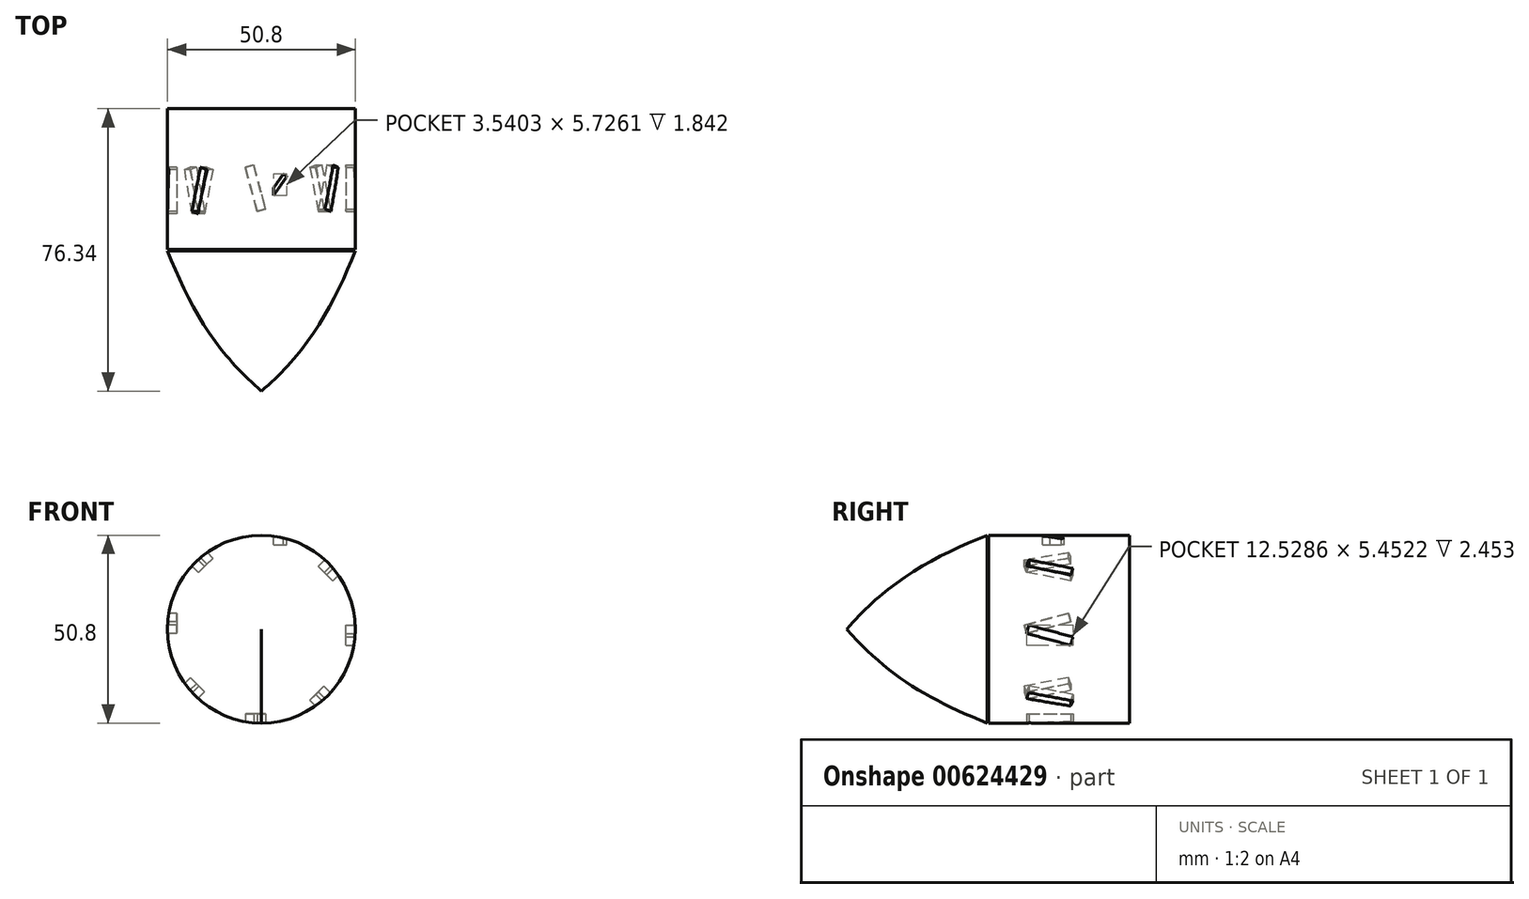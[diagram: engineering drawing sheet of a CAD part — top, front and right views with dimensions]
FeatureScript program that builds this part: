
annotation { "Feature Type Name" : "Feature", "Feature Type Description" : "" }
export const myFeature = defineFeature(function(context is Context, id is Id, definition is map)
    precondition{}
    {
        {
            var Q0;
            Q0=qCreatedBy(makeId("Front.planeOp"),FACE);
            var sketch = newSketch(context, id + "F0", { "sketchPlane" : qUnion([Q0])});
            skCircle(sketch, "E0", {"center": v(0, 0) * mm, "radius": 25.4 * mm});
            skSolve(sketch);
        }
        {
            var Q0;
            Q0=makeQuery(id+"F0.imprint","IMPRINT",FACE,{"disambiguationData":[TD([[makeQuery(id+"F0.imprint","IMPRINT",EDGE,{"derivedFrom":sQuery(id+"F0.wireOp",EDGE,"E0")}),1.0]])]});
            extrude(context, id + "F1", {"entities" : qUnion([Q0]), "depth" : 38.1 * mm, "offsetDistance" : 25.4 * mm});
        }
        {
            var Q0;
            Q0=qCreatedBy(makeId("Right.planeOp"),FACE);
            var sketch = newSketch(context, id + "F2", { "sketchPlane" : qUnion([Q0])});
            skLineSegment(sketch, "E1", {"start": v(-76.34, 0) * mm, "end": v(-38.37, 0) * mm});
            skLineSegment(sketch, "E2", {"start": v(-38.37, 0) * mm, "end": v(-38.37, 25.4) * mm});
            skLineSegment(sketch, "E3", {"start": v(-38.37, 0) * mm, "end": v(-38.37, -25.4) * mm});
            skFitSpline(sketch, "E4", {"points": [v(-38.37, -25.4) * mm, v(-76.34, 0) * mm], "startDerivative": vector(-48.65, 19.21) * mm, "endDerivative": vector(-31.18, 36.31) * mm});
            skSolve(sketch);
        }
        {
            var Q0;
            Q0=makeQuery(id+"F2.imprint","IMPRINT",FACE,{"disambiguationData":[TD([[makeQuery(id+"F2.imprint","IMPRINT",EDGE,{"derivedFrom":sQuery(id+"F2.wireOp",EDGE,"E1")}),-1.0]])]});
            var Q1;
            Q1=sQuery(id+"F2.wireOp",EDGE,"E1");
            revolve(context, id + "F3", {"entities" : qUnion([Q0]), "axis" : qUnion([Q1]), "revolveType" : RevolveType.FULL});
        }
        {
            var Q0;
            Q0=qCreatedBy(makeId("Right.planeOp"),FACE);
            cPlane(context, id + "F4", {"entities" : qUnion([Q0]), "cplaneType" : CPlaneType.OFFSET, "offset" : 25.4 * mm, "width" : 152.4 * mm, "height" : 152.4 * mm});
        }
        {
            var Q0;
            Q0=qCreatedBy(makeId("Right.planeOp"),FACE);
            cPlane(context, id + "F5", {"entities" : qUnion([Q0]), "cplaneType" : CPlaneType.OFFSET, "offset" : 25.4 * mm, "oppositeDirection" : true, "width" : 152.4 * mm, "height" : 152.4 * mm});
        }
        {
            var Q0;
            Q0=qCreatedBy(makeId("Top.planeOp"),FACE);
            cPlane(context, id + "F6", {"entities" : qUnion([Q0]), "cplaneType" : CPlaneType.OFFSET, "offset" : 25.4 * mm, "width" : 152.4 * mm, "height" : 152.4 * mm});
        }
        {
            var Q0;
            Q0=qCreatedBy(makeId("Top.planeOp"),FACE);
            cPlane(context, id + "F7", {"entities" : qUnion([Q0]), "cplaneType" : CPlaneType.OFFSET, "offset" : 25.4 * mm, "oppositeDirection" : true, "width" : 152.4 * mm, "height" : 152.4 * mm});
        }
        {
            var Q0;
            Q0=qCreatedBy(makeId("Right.planeOp"),FACE);
            var Q1;
            Q1=qCreatedBy(makeId("Top.planeOp"),FACE);
            cPlane(context, id + "F8", {"entities" : qUnion([Q0, Q1]), "cplaneType" : CPlaneType.MID_PLANE, "offset" : 25.4 * mm, "width" : 152.4 * mm, "height" : 152.4 * mm});
        }
        {
            var Q0;
            Q0=qCreatedBy(makeId("Right.planeOp"),FACE);
            var Q1;
            Q1=qCreatedBy(makeId("Top.planeOp"),FACE);
            cPlane(context, id + "F9", {"entities" : qUnion([Q0, Q1]), "cplaneType" : CPlaneType.MID_PLANE, "offset" : 25.4 * mm, "flipAlignment" : true, "width" : 152.4 * mm, "height" : 152.4 * mm});
        }
        {
            var Q0;
            Q0=qCreatedBy(id+"F8.planeOp",FACE);
            cPlane(context, id + "F10", {"entities" : qUnion([Q0]), "cplaneType" : CPlaneType.OFFSET, "offset" : 25.4 * mm, "width" : 152.4 * mm, "height" : 152.4 * mm});
        }
        {
            var Q0;
            Q0=qCreatedBy(id+"F8.planeOp",FACE);
            cPlane(context, id + "F11", {"entities" : qUnion([Q0]), "cplaneType" : CPlaneType.OFFSET, "offset" : 25.4 * mm, "oppositeDirection" : true, "width" : 152.4 * mm, "height" : 152.4 * mm});
        }
        {
            var Q0;
            Q0=qCreatedBy(id+"F9.planeOp",FACE);
            cPlane(context, id + "F12", {"entities" : qUnion([Q0]), "cplaneType" : CPlaneType.OFFSET, "offset" : 25.4 * mm, "width" : 152.4 * mm, "height" : 152.4 * mm});
        }
        {
            var Q0;
            Q0=qCreatedBy(id+"F9.planeOp",FACE);
            cPlane(context, id + "F13", {"entities" : qUnion([Q0]), "cplaneType" : CPlaneType.OFFSET, "offset" : 25.4 * mm, "oppositeDirection" : true, "width" : 152.4 * mm, "height" : 152.4 * mm});
        }
        {
            var Q0;
            Q0=qCreatedBy(id+"F12.planeOp",FACE);
            var sketch = newSketch(context, id + "F14", { "sketchPlane" : qUnion([Q0])});
            skLineSegment(sketch, "E5.bottom", {"start": v(-15.84, -4.36) * mm, "end": v(-27.76, -1.17) * mm});
            skLineSegment(sketch, "E5.top", {"start": v(-15.23, -2.1) * mm, "end": v(-27.16, 1.09) * mm});
            skLineSegment(sketch, "E5.left", {"start": v(-15.84, -4.36) * mm, "end": v(-15.23, -2.1) * mm});
            skLineSegment(sketch, "E5.right", {"start": v(-27.76, -1.17) * mm, "end": v(-27.16, 1.09) * mm});
            skPoint(sketch, "E5.middle", {"position": v(-21.59, 0) * mm});
            skSolve(sketch);
        }
        {
            var Q0;
            Q0=qCreatedBy(id+"F11.planeOp",FACE);
            var sketch = newSketch(context, id + "F15", { "sketchPlane" : qUnion([Q0])});
            skLineSegment(sketch, "E6.bottom", {"start": v(-15.84, 2.03) * mm, "end": v(-27.76, -1.17) * mm});
            skLineSegment(sketch, "E6.top", {"start": v(-16.44, 4.28) * mm, "end": v(-28.37, 1.09) * mm});
            skLineSegment(sketch, "E6.left", {"start": v(-15.84, 2.03) * mm, "end": v(-16.44, 4.28) * mm});
            skLineSegment(sketch, "E6.right", {"start": v(-27.76, -1.17) * mm, "end": v(-28.37, 1.09) * mm});
            skPoint(sketch, "E6.middle", {"position": v(-21.59, 0) * mm});
            skSolve(sketch);
        }
        {
            var Q0;
            Q0=qCreatedBy(id+"F5.planeOp",FACE);
            var sketch = newSketch(context, id + "F16", { "sketchPlane" : qUnion([Q0])});
            skLineSegment(sketch, "E7.bottom", {"start": v(-15.84, 2.03) * mm, "end": v(-27.76, -1.17) * mm});
            skLineSegment(sketch, "E7.top", {"start": v(-16.44, 4.28) * mm, "end": v(-28.37, 1.09) * mm});
            skLineSegment(sketch, "E7.left", {"start": v(-15.84, 2.03) * mm, "end": v(-16.44, 4.28) * mm});
            skLineSegment(sketch, "E7.right", {"start": v(-27.76, -1.17) * mm, "end": v(-28.37, 1.09) * mm});
            skPoint(sketch, "E7.middle", {"position": v(-22.1, 1.56) * mm});
            skSolve(sketch);
        }
        {
            var Q0;
            Q0=qCreatedBy(id+"F13.planeOp",FACE);
            var sketch = newSketch(context, id + "F17", { "sketchPlane" : qUnion([Q0])});
            skLineSegment(sketch, "E8.bottom", {"start": v(-15.84, 2.03) * mm, "end": v(-27.76, -1.17) * mm});
            skLineSegment(sketch, "E8.top", {"start": v(-16.44, 4.28) * mm, "end": v(-28.37, 1.09) * mm});
            skLineSegment(sketch, "E8.left", {"start": v(-15.84, 2.03) * mm, "end": v(-16.44, 4.28) * mm});
            skLineSegment(sketch, "E8.right", {"start": v(-27.76, -1.17) * mm, "end": v(-28.37, 1.09) * mm});
            skPoint(sketch, "E8.middle", {"position": v(-22.1, 1.56) * mm});
            skSolve(sketch);
        }
        {
            var Q0;
            Q0=qCreatedBy(id+"F7.planeOp",FACE);
            var sketch = newSketch(context, id + "F18", { "sketchPlane" : qUnion([Q0])});
            skLineSegment(sketch, "E9.bottom", {"start": v(-1.17, -27.76) * mm, "end": v(-4.36, -15.84) * mm});
            skLineSegment(sketch, "E9.top", {"start": v(1.09, -27.16) * mm, "end": v(-2.1, -15.23) * mm});
            skLineSegment(sketch, "E9.left", {"start": v(-1.17, -27.76) * mm, "end": v(1.09, -27.16) * mm});
            skLineSegment(sketch, "E9.right", {"start": v(-4.36, -15.84) * mm, "end": v(-2.1, -15.23) * mm});
            skPoint(sketch, "E9.middle", {"position": v(-1.64, -21.5) * mm});
            skSolve(sketch);
        }
        {
            var Q0;
            Q0=qCreatedBy(id+"F10.planeOp",FACE);
            var sketch = newSketch(context, id + "F19", { "sketchPlane" : qUnion([Q0])});
            skLineSegment(sketch, "E10.bottom", {"start": v(-15.84, -4.36) * mm, "end": v(-27.76, -1.17) * mm});
            skLineSegment(sketch, "E10.top", {"start": v(-15.23, -2.1) * mm, "end": v(-27.16, 1.09) * mm});
            skLineSegment(sketch, "E10.left", {"start": v(-15.84, -4.36) * mm, "end": v(-15.23, -2.1) * mm});
            skLineSegment(sketch, "E10.right", {"start": v(-27.76, -1.17) * mm, "end": v(-27.16, 1.09) * mm});
            skPoint(sketch, "E10.middle", {"position": v(-21.5, -1.64) * mm});
            skSolve(sketch);
        }
        {
            var Q0;
            Q0=qCreatedBy(id+"F4.planeOp",FACE);
            var sketch = newSketch(context, id + "F20", { "sketchPlane" : qUnion([Q0])});
            skLineSegment(sketch, "E11.bottom", {"start": v(-15.84, -4.36) * mm, "end": v(-27.76, -1.17) * mm});
            skLineSegment(sketch, "E11.top", {"start": v(-15.23, -2.1) * mm, "end": v(-27.16, 1.09) * mm});
            skLineSegment(sketch, "E11.left", {"start": v(-15.84, -4.36) * mm, "end": v(-15.23, -2.1) * mm});
            skLineSegment(sketch, "E11.right", {"start": v(-27.76, -1.17) * mm, "end": v(-27.16, 1.09) * mm});
            skPoint(sketch, "E11.middle", {"position": v(-21.5, -1.64) * mm});
            skSolve(sketch);
        }
        {
            var Q0;
            Q0=qCreatedBy(id+"F6.planeOp",FACE);
            var sketch = newSketch(context, id + "F21", { "sketchPlane" : qUnion([Q0])});
            skLineSegment(sketch, "E12.bottom", {"start": v(-1.17, -27.76) * mm, "end": v(5.91, -17.65) * mm});
            skLineSegment(sketch, "E12.top", {"start": v(0.75, -29.1) * mm, "end": v(7.83, -19) * mm});
            skLineSegment(sketch, "E12.left", {"start": v(-1.17, -27.76) * mm, "end": v(0.75, -29.1) * mm});
            skLineSegment(sketch, "E12.right", {"start": v(5.91, -17.65) * mm, "end": v(7.83, -19) * mm});
            skPoint(sketch, "E12.middle", {"position": v(3.33, -23.38) * mm});
            skLineSegment(sketch, "E13", {"start": v(3.33, -23.38) * mm, "end": v(3.33, -4.06) * mm});
            skLineSegment(sketch, "E14", {"start": v(3.33, -23.38) * mm, "end": v(6.87, -18.32) * mm});
            skLineSegment(sketch, "E15", {"start": v(6.87, -18.32) * mm, "end": v(14.25, -7.78) * mm});
            skSolve(sketch);
        }
        {
            var Q0;
            Q0=makeQuery(id+"F16.imprint","IMPRINT",FACE,{"disambiguationData":[TD([[makeQuery(id+"F16.imprint","IMPRINT",EDGE,{"derivedFrom":sQuery(id+"F16.wireOp",EDGE,"E7.bottom")}),-1.0]])]});
            extrude(context, id + "F22", {"entities" : qUnion([Q0]), "operationType" : NewBodyOperationType.REMOVE, "depth" : 2.54 * mm, "offsetDistance" : 25.4 * mm});
        }
        {
            var Q0;
            Q0=makeQuery(id+"F15.imprint","IMPRINT",FACE,{"disambiguationData":[TD([[makeQuery(id+"F15.imprint","IMPRINT",EDGE,{"derivedFrom":sQuery(id+"F15.wireOp",EDGE,"E6.bottom")}),-1.0]])]});
            extrude(context, id + "F23", {"entities" : qUnion([Q0]), "operationType" : NewBodyOperationType.REMOVE, "depth" : 2.54 * mm, "offsetDistance" : 25.4 * mm});
        }
        {
            var Q0;
            Q0=makeQuery(id+"F21.imprint","IMPRINT",FACE,{"disambiguationData":[TD([[makeQuery(id+"F21.imprint","IMPRINT",EDGE,{"derivedFrom":sQuery(id+"F21.wireOp",EDGE,"E12.bottom")}),-1.0]])]});
            extrude(context, id + "F24", {"entities" : qUnion([Q0]), "operationType" : NewBodyOperationType.REMOVE, "oppositeDirection" : true, "depth" : 2.54 * mm, "offsetDistance" : 25.4 * mm});
        }
        {
            var Q0;
            Q0=makeQuery(id+"F14.imprint","IMPRINT",FACE,{"disambiguationData":[TD([[makeQuery(id+"F14.imprint","IMPRINT",EDGE,{"derivedFrom":sQuery(id+"F14.wireOp",EDGE,"E5.bottom")}),-1.0]])]});
            extrude(context, id + "F25", {"entities" : qUnion([Q0]), "operationType" : NewBodyOperationType.REMOVE, "oppositeDirection" : true, "depth" : 2.54 * mm, "offsetDistance" : 25.4 * mm});
        }
        {
            var Q0;
            Q0=makeQuery(id+"F20.imprint","IMPRINT",FACE,{"disambiguationData":[TD([[makeQuery(id+"F20.imprint","IMPRINT",EDGE,{"derivedFrom":sQuery(id+"F20.wireOp",EDGE,"E11.bottom")}),-1.0]])]});
            extrude(context, id + "F26", {"entities" : qUnion([Q0]), "operationType" : NewBodyOperationType.REMOVE, "oppositeDirection" : true, "depth" : 2.54 * mm, "offsetDistance" : 25.4 * mm});
        }
        {
            var Q0;
            Q0=makeQuery(id+"F19.imprint","IMPRINT",FACE,{"disambiguationData":[TD([[makeQuery(id+"F19.imprint","IMPRINT",EDGE,{"derivedFrom":sQuery(id+"F19.wireOp",EDGE,"E10.bottom")}),-1.0]])]});
            extrude(context, id + "F27", {"entities" : qUnion([Q0]), "operationType" : NewBodyOperationType.REMOVE, "oppositeDirection" : true, "depth" : 2.54 * mm, "offsetDistance" : 25.4 * mm});
        }
        {
            var Q0;
            Q0=makeQuery(id+"F18.imprint","IMPRINT",FACE,{"disambiguationData":[TD([[makeQuery(id+"F18.imprint","IMPRINT",EDGE,{"derivedFrom":sQuery(id+"F18.wireOp",EDGE,"E9.bottom")}),-1.0]])]});
            extrude(context, id + "F28", {"entities" : qUnion([Q0]), "operationType" : NewBodyOperationType.REMOVE, "depth" : 2.54 * mm, "offsetDistance" : 25.4 * mm});
        }
        {
            var Q0;
            Q0=makeQuery(id+"F17.imprint","IMPRINT",FACE,{"disambiguationData":[TD([[makeQuery(id+"F17.imprint","IMPRINT",EDGE,{"derivedFrom":sQuery(id+"F17.wireOp",EDGE,"E8.bottom")}),-1.0]])]});
            extrude(context, id + "F29", {"entities" : qUnion([Q0]), "operationType" : NewBodyOperationType.REMOVE, "depth" : 2.54 * mm, "offsetDistance" : 25.4 * mm});
        }
    });
